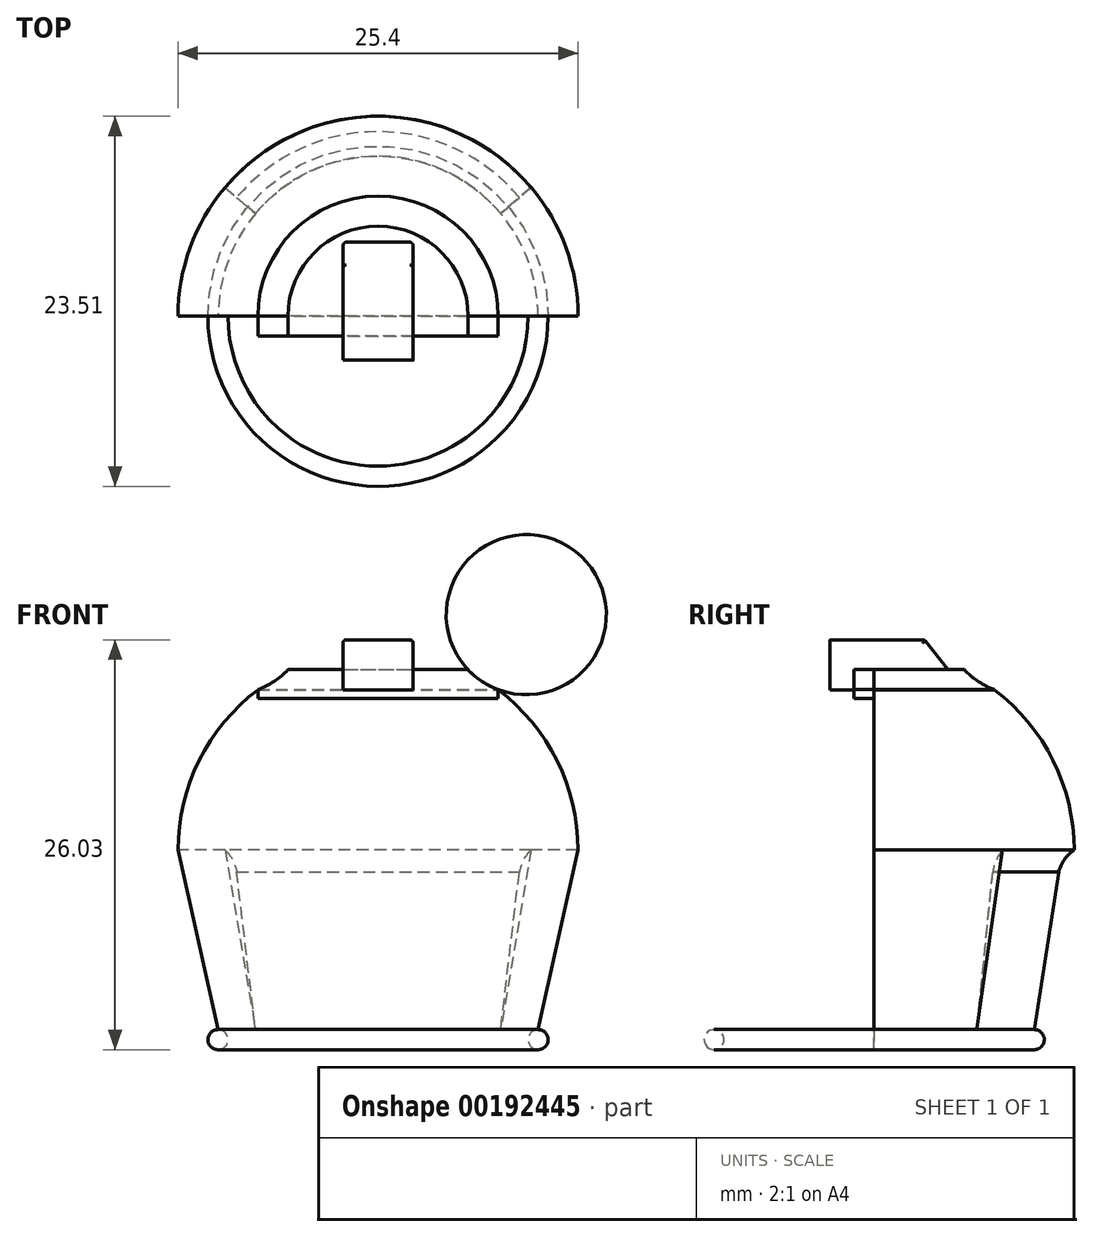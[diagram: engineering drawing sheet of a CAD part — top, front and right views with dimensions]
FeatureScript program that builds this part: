
annotation { "Feature Type Name" : "Feature", "Feature Type Description" : "" }
export const myFeature = defineFeature(function(context is Context, id is Id, definition is map)
    precondition{}
    {
        {
            var Q0;
            Q0=qCreatedBy(makeId("Right.planeOp"),FACE);
            var sketch = newSketch(context, id + "F0", { "sketchPlane" : qUnion([Q0])});
            skLineSegment(sketch, "E0", {"start": v(0, 0) * mm, "end": v(0, 25.4) * mm});
            skSolve(sketch);
        }
        {
            var Q0;
            Q0=qCreatedBy(makeId("Right.planeOp"),FACE);
            var sketch = newSketch(context, id + "F1", { "sketchPlane" : qUnion([Q0])});
            skLineSegment(sketch, "E1", {"start": v(0, 12.7) * mm, "end": v(0, 22.86) * mm});
            skArc(sketch, "E2", {"start": v(12.7, 12.7) * mm, "mid": v(11.36, 18.38) * mm, "end": v(7.63, 22.86) * mm});
            skLineSegment(sketch, "E3", {"start": v(0, 12.7) * mm, "end": v(12.7, 12.7) * mm});
            skLineSegment(sketch, "E4", {"start": v(0, 22.86) * mm, "end": v(7.63, 22.86) * mm});
            skSolve(sketch);
        }
        {
            var Q0;
            Q0 = qSketchRegion(id + "F1", true);
            var Q1;
            Q1=sQuery(id+"F1.wireOp",EDGE,"E1");
            revolve(context, id + "F2", {"entities" : qUnion([Q0]), "axis" : qUnion([Q1]), "revolveType" : RevolveType.SYMMETRIC, "angle" : 180 * degree});
        }
        {
            var Q0;
            Q0=qCreatedBy(makeId("Right.planeOp"),FACE);
            var sketch = newSketch(context, id + "F3", { "sketchPlane" : qUnion([Q0])});
            skLineSegment(sketch, "E5", {"start": v(0, 0) * mm, "end": v(10.16, 0) * mm});
            skLineSegment(sketch, "E6", {"start": v(10.16, 0) * mm, "end": v(10.16, 1.27) * mm});
            skLineSegment(sketch, "E7", {"start": v(0, 0) * mm, "end": v(0, 12.7) * mm});
            skLineSegment(sketch, "E8", {"start": v(0, 12.7) * mm, "end": v(12.7, 12.7) * mm});
            skLineSegment(sketch, "E9", {"start": v(10.16, 1.27) * mm, "end": v(11.72, 11.3) * mm});
            skArc(sketch, "E10", {"start": v(12.7, 12.7) * mm, "mid": v(12.1, 12.08) * mm, "end": v(11.72, 11.3) * mm});
            skSolve(sketch);
        }
        {
            var Q0;
            Q0 = qSketchRegion(id + "F3", true);
            var Q1;
            Q1=sQuery(id+"F0.wireOp",EDGE,"E0");
            revolve(context, id + "F4", {"operationType" : NewBodyOperationType.ADD, "entities" : qUnion([Q0]), "axis" : qUnion([Q1]), "revolveType" : RevolveType.SYMMETRIC, "angle" : 100 * degree});
        }
        {
            var Q0;
            Q0=qCreatedBy(makeId("Right.planeOp"),FACE);
            var sketch = newSketch(context, id + "F5", { "sketchPlane" : qUnion([Q0])});
            skLineSegment(sketch, "E11", {"start": v(-2.8, 25.4) * mm, "end": v(-2.8, 22.86) * mm});
            skLineSegment(sketch, "E12", {"start": v(5.71, 22.86) * mm, "end": v(-2.8, 22.86) * mm});
            skLineSegment(sketch, "E13", {"start": v(3.18, 26.03) * mm, "end": v(-2.8, 26.03) * mm});
            skLineSegment(sketch, "E14", {"start": v(-2.8, 26.03) * mm, "end": v(-2.8, 25.4) * mm});
            skLineSegment(sketch, "E15", {"start": v(3.18, 26.03) * mm, "end": v(5.71, 22.86) * mm});
            skSolve(sketch);
        }
        {
            var Q0;
            Q0=qCreatedBy(makeId("Right.planeOp"),FACE);
            var sketch = newSketch(context, id + "F6", { "sketchPlane" : qUnion([Q0])});
            skLineSegment(sketch, "E16", {"start": v(0, 24.13) * mm, "end": v(5.72, 24.13) * mm});
            skArc(sketch, "E17", {"start": v(5.72, 24.13) * mm, "mid": v(6.6, 23.4) * mm, "end": v(7.63, 22.87) * mm});
            skLineSegment(sketch, "E18", {"start": v(7.63, 22.87) * mm, "end": v(7.63, 22.31) * mm});
            skLineSegment(sketch, "E19", {"start": v(7.63, 22.31) * mm, "end": v(0, 22.31) * mm});
            skLineSegment(sketch, "E20", {"start": v(0, 22.31) * mm, "end": v(0, 24.13) * mm});
            skSolve(sketch);
        }
        {
            var Q0;
            Q0 = qSketchRegion(id + "F6", true);
            var Q1;
            Q1=sQuery(id+"F6.wireOp",EDGE,"E20");
            revolve(context, id + "F7", {"operationType" : NewBodyOperationType.ADD, "entities" : qUnion([Q0]), "axis" : qUnion([Q1]), "revolveType" : RevolveType.SYMMETRIC, "angle" : 180 * degree});
        }
        {
            var Q0;
            Q0 = qSketchRegion(id + "F5", true);
            extrude(context, id + "F8", {"entities" : qUnion([Q0]), "operationType" : NewBodyOperationType.ADD, "endBound" : BoundingType.SYMMETRIC, "depth" : 4.44 * mm});
        }
        {
            var Q0;
            Q0=qCreatedBy(makeId("Front.planeOp"),FACE);
            var sketch = newSketch(context, id + "F9", { "sketchPlane" : qUnion([Q0])});
            skLineSegment(sketch, "E21", {"start": v(0, 0) * mm, "end": v(0, 12.7) * mm});
            skLineSegment(sketch, "E22", {"start": v(0, 0) * mm, "end": v(-10.15, 0) * mm});
            skLineSegment(sketch, "E23", {"start": v(-10.15, 0) * mm, "end": v(-10.15, 1.27) * mm});
            skLineSegment(sketch, "E24", {"start": v(0, 12.7) * mm, "end": v(-12.7, 12.7) * mm});
            skLineSegment(sketch, "E25", {"start": v(-12.7, 12.7) * mm, "end": v(-10.15, 1.27) * mm});
            skSolve(sketch);
        }
        {
            var Q0;
            Q0=qCreatedBy(makeId("Right.planeOp"),FACE);
            var sketch = newSketch(context, id + "F10", { "sketchPlane" : qUnion([Q0])});
            skCircle(sketch, "E26", {"center": v(10.17, 0.64) * mm, "radius": 0.64 * mm});
            skSolve(sketch);
        }
        {
            var Q0;
            Q0 = qSketchRegion(id + "F10", true);
            var Q1;
            Q1=sQuery(id+"F9.wireOp",EDGE,"E21");
            revolve(context, id + "F11", {"operationType" : NewBodyOperationType.ADD, "entities" : qUnion([Q0]), "axis" : qUnion([Q1]), "revolveType" : RevolveType.FULL});
        }
        {
            var Q0;
            Q0 = qSketchRegion(id + "F9", true);
            var Q1;
            Q1=makeQuery(id+"F4.opRevolve","CAP_EDGE",EDGE,{"disambiguationData":[OSD([sQuery(id+"F3.wireOp",EDGE,"E7")])],"isStart":true});
            revolve(context, id + "F12", {"operationType" : NewBodyOperationType.ADD, "entities" : qUnion([Q0]), "axis" : qUnion([Q1]), "revolveType" : RevolveType.ONE_DIRECTION, "oppositeDirection" : true, "angle" : 40 * degree});
        }
        {
            var Q0;
            Q0=qCreatedBy(makeId("Front.planeOp"),FACE);
            var sketch = newSketch(context, id + "F13", { "sketchPlane" : qUnion([Q0])});
            skLineSegment(sketch, "E27", {"start": v(0, 0) * mm, "end": v(10.16, 0) * mm});
            skLineSegment(sketch, "E28", {"start": v(10.16, 0) * mm, "end": v(10.16, 1.27) * mm});
            skLineSegment(sketch, "E29", {"start": v(0, 0) * mm, "end": v(0, 12.7) * mm});
            skLineSegment(sketch, "E30", {"start": v(0, 12.7) * mm, "end": v(12.7, 12.7) * mm});
            skLineSegment(sketch, "E31", {"start": v(12.7, 12.7) * mm, "end": v(10.16, 1.27) * mm});
            skSolve(sketch);
        }
        {
            var Q0;
            Q0=makeQuery(id+"F13.imprint","IMPRINT",FACE,{"disambiguationData":[TD([[makeQuery(id+"F13.imprint","IMPRINT",EDGE,{"derivedFrom":sQuery(id+"F13.wireOp",EDGE,"E27")}),1.0]])]});
            var Q1;
            Q1=sQuery(id+"F13.wireOp",EDGE,"E29");
            revolve(context, id + "F14", {"operationType" : NewBodyOperationType.ADD, "entities" : qUnion([Q0]), "axis" : qUnion([Q1]), "revolveType" : RevolveType.ONE_DIRECTION, "angle" : 40 * degree});
        }
        {
            var Q0;
            Q0=makeQuery(id+"F8.opExtrude","CAP_EDGE",EDGE,{"disambiguationData":[OSD([sQuery(id+"F5.wireOp",EDGE,"E15")])],"isStart":true});
            fillet(context, id + "F15", {"entities" : qUnion([Q0]), "radius" : 0.2 * mm, "tangentPropagation" : true, "allowEdgeOverflow" : false});
        }
        {
            var Q0;
            Q0=makeQuery(id+"F8.opExtrude","CAP_EDGE",EDGE,{"disambiguationData":[OSD([sQuery(id+"F5.wireOp",EDGE,"E15")])],"isStart":false});
            fillet(context, id + "F16", {"entities" : qUnion([Q0]), "radius" : 0.2 * mm, "tangentPropagation" : true, "allowEdgeOverflow" : false});
        }
        {
            var Q0;
            Q0=makeQuery(id+"F8.opExtrude","SWEPT_EDGE",EDGE,{"disambiguationData":[OSD([sQuery(id+"F5.wireOp",EDGE,"E13"),sQuery(id+"F5.wireOp",EDGE,"E15")])]});
            fillet(context, id + "F17", {"entities" : qUnion([Q0]), "radius" : 0.2 * mm, "tangentPropagation" : true, "allowEdgeOverflow" : false});
        }
        {
            var Q0;
            Q0=qCreatedBy(makeId("Front.planeOp"),FACE);
            var sketch = newSketch(context, id + "F18", { "sketchPlane" : qUnion([Q0])});
            skLineSegment(sketch, "E32", {"start": v(0, 24.14) * mm, "end": v(5.72, 24.14) * mm});
            skArc(sketch, "E33", {"start": v(5.72, 24.14) * mm, "mid": v(6.6, 23.4) * mm, "end": v(7.63, 22.87) * mm});
            skLineSegment(sketch, "E34", {"start": v(7.63, 22.87) * mm, "end": v(7.63, 22.31) * mm});
            skLineSegment(sketch, "E35", {"start": v(7.63, 22.31) * mm, "end": v(0, 22.31) * mm});
            skLineSegment(sketch, "E36.MirrorCS", {"start": v(0, 24.14) * mm, "end": v(-5.72, 24.14) * mm});
            skArc(sketch, "E37.MirrorCS", {"start": v(-5.72, 24.14) * mm, "mid": v(-6.6, 23.4) * mm, "end": v(-7.63, 22.87) * mm});
            skLineSegment(sketch, "E38.MirrorCS", {"start": v(-7.63, 22.87) * mm, "end": v(-7.63, 22.31) * mm});
            skLineSegment(sketch, "E39.MirrorCS", {"start": v(-7.63, 22.31) * mm, "end": v(0, 22.31) * mm});
            skSolve(sketch);
        }
        {
            var Q0;
            Q0 = qSketchRegion(id + "F18", true);
            extrude(context, id + "F19", {"entities" : qUnion([Q0]), "operationType" : NewBodyOperationType.ADD, "depth" : 1.27 * mm});
        }
    });
